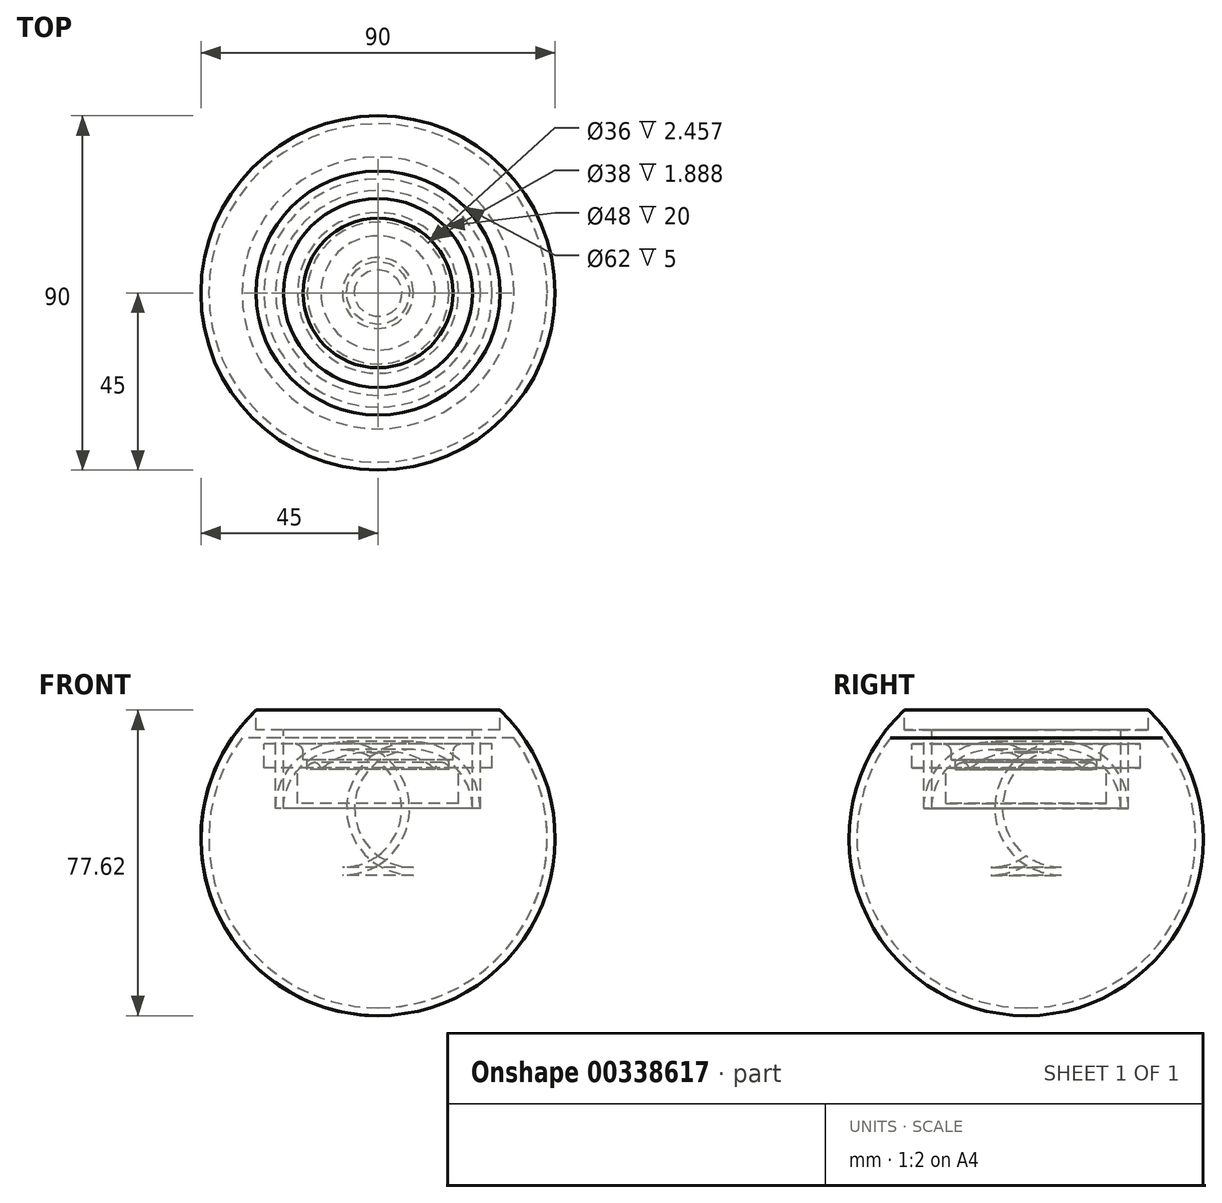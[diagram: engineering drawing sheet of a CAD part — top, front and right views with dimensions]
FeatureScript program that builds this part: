
annotation { "Feature Type Name" : "Feature", "Feature Type Description" : "" }
export const myFeature = defineFeature(function(context is Context, id is Id, definition is map)
    precondition{}
    {
        {
            var Q0;
            Q0=qCreatedBy(makeId("Front.planeOp"),FACE);
            var sketch = newSketch(context, id + "F0", { "sketchPlane" : qUnion([Q0])});
            skLineSegment(sketch, "E0", {"start": v(24, 29.04) * mm, "end": v(31, 29.04) * mm});
            skLineSegment(sketch, "E1", {"start": v(31, 29.04) * mm, "end": v(31, 34.04) * mm});
            skLineSegment(sketch, "E2", {"start": v(24, 29.04) * mm, "end": v(24, 9.04) * mm});
            skLineSegment(sketch, "E3", {"start": v(24, 9.04) * mm, "end": v(24, 9.04) * mm});
            skLineSegment(sketch, "E4", {"start": v(9, -5.96) * mm, "end": v(0, -5.96) * mm});
            skPoint(sketch, "E5.visualSharp", {"position": v(24, -5.96) * mm});
            skArc(sketch, "E5.filletArc", {"start": v(9, -5.96) * mm, "mid": v(19.6, -1.57) * mm, "end": v(24, 9.04) * mm});
            skLineSegment(sketch, "E6", {"start": v(0, 64.62) * mm, "end": v(0, -67.22) * mm, "construction": true});
            skArc(sketch, "E7", {"start": v(0, -43.58) * mm, "mid": v(41.8, -15.27) * mm, "end": v(31, 34.04) * mm});
            skLineSegment(sketch, "E8", {"start": v(45, 38.22) * mm, "end": v(45, -53.52) * mm, "construction": true});
            skPoint(sketch, "E9.visualSharp", {"position": v(33, 28.99) * mm});
            skLineSegment(sketch, "E10", {"start": v(0, -5.96) * mm, "end": v(0, -7.96) * mm});
            skLineSegment(sketch, "E11", {"start": v(0, -41.58) * mm, "end": v(0, -43.58) * mm});
            skArc(sketch, "E12.0", {"start": v(0, -41.58) * mm, "mid": v(38.4, -17.91) * mm, "end": v(34.53, 27.04) * mm});
            skLineSegment(sketch, "E12.1", {"start": v(9, -7.96) * mm, "end": v(0, -7.96) * mm});
            skArc(sketch, "E12.2", {"start": v(9, -7.96) * mm, "mid": v(21.02, -2.98) * mm, "end": v(26, 9.04) * mm});
            skLineSegment(sketch, "E12.3", {"start": v(26, 27.04) * mm, "end": v(26, 9.04) * mm});
            skLineSegment(sketch, "E12.4", {"start": v(26, 27.04) * mm, "end": v(34.53, 27.04) * mm});
            skSolve(sketch);
        }
        {
            var Q0;
            Q0 = qSketchRegion(id + "F0", true);
            var Q1;
            Q1=sQuery(id+"F0.wireOp",EDGE,"E6");
            revolve(context, id + "F1", {"entities" : qUnion([Q0]), "axis" : qUnion([Q1]), "revolveType" : RevolveType.FULL});
        }
        {
            var Q0;
            Q0=qCreatedBy(makeId("Front.planeOp"),FACE);
            var sketch = newSketch(context, id + "F2", { "sketchPlane" : qUnion([Q0])});
            skLineSegment(sketch, "E13", {"start": v(29, 25.43) * mm, "end": v(21.1, 25.43) * mm});
            skLineSegment(sketch, "E14", {"start": v(19, 23.33) * mm, "end": v(19, 21.44) * mm});
            skLineSegment(sketch, "E15", {"start": v(19, 21.44) * mm, "end": v(18, 21.44) * mm});
            skPoint(sketch, "E16.visualSharp", {"position": v(19, 25.43) * mm});
            skArc(sketch, "E16.filletArc", {"start": v(21.1, 25.43) * mm, "mid": v(19.62, 24.81) * mm, "end": v(19, 23.33) * mm});
            skLineSegment(sketch, "E17", {"start": v(18, 21.44) * mm, "end": v(18, 18.98) * mm});
            skArc(sketch, "E18", {"start": v(18, 18.98) * mm, "mid": v(16.25, 20.73) * mm, "end": v(14.5, 18.98) * mm});
            skFitSpline(sketch, "E19", {"points": [v(14.5, 18.98) * mm, v(0, 23.2) * mm], "startDerivative": vector(-13.54, 12.11) * mm, "endDerivative": vector(-15.48, -1.84) * mm});
            skLineSegment(sketch, "E20", {"start": v(0, 43.03) * mm, "end": v(0, -3.84) * mm, "construction": true});
            skLineSegment(sketch, "E21", {"start": v(29, 19.43) * mm, "end": v(20.42, 19.43) * mm});
            skLineSegment(sketch, "E22", {"start": v(20.42, 19.43) * mm, "end": v(20.42, 10.3) * mm});
            skLineSegment(sketch, "E23", {"start": v(20.42, 10.3) * mm, "end": v(0, 10.3) * mm});
            skLineSegment(sketch, "E24", {"start": v(0, 10.3) * mm, "end": v(0, 23.2) * mm});
            skLineSegment(sketch, "E25", {"start": v(29, 19.43) * mm, "end": v(29, 25.43) * mm});
            skSolve(sketch);
        }
        {
            var Q0;
            Q0=makeQuery(id+"F2.imprint","IMPRINT",FACE,{"disambiguationData":[TD([[makeQuery(id+"F2.imprint","IMPRINT",EDGE,{"derivedFrom":sQuery(id+"F2.wireOp",EDGE,"E13")}),1.0]])]});
            var Q1;
            Q1=sQuery(id+"F2.wireOp",EDGE,"E20");
            revolve(context, id + "F3", {"entities" : qUnion([Q0]), "axis" : qUnion([Q1]), "revolveType" : RevolveType.FULL});
        }
        {
            var Q0;
            Q0=sQuery(id+"F2.wireOp",EDGE,"E19");
            var Q1;
            Q1=sQuery(id+"F2.wireOp",EDGE,"E18");
            var Q2;
            Q2=sQuery(id+"F2.wireOp",EDGE,"E20");
            revolve(context, id + "F4", {"bodyType" : ToolBodyType.SURFACE, "surfaceEntities" : qUnion([Q0, Q1]), "axis" : qUnion([Q2]), "revolveType" : RevolveType.FULL});
        }
    });
